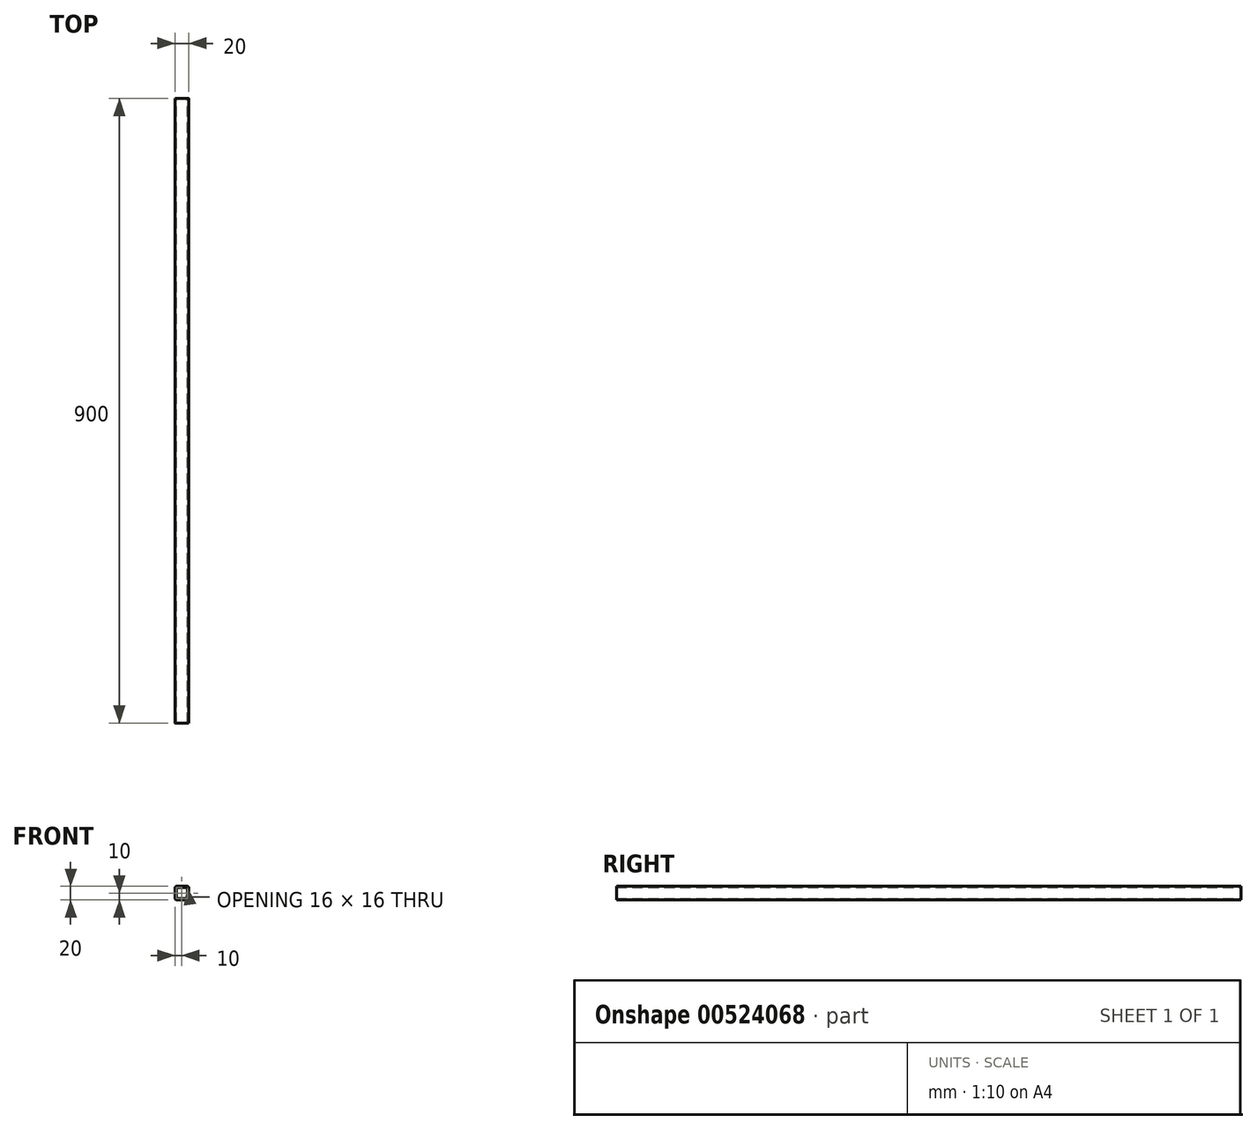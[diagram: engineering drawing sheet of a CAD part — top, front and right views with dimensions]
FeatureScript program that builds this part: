
annotation { "Feature Type Name" : "Feature", "Feature Type Description" : "" }
export const myFeature = defineFeature(function(context is Context, id is Id, definition is map)
    precondition{}
    {
        {
            assignVariable(context, id + "F0", {"name" : "R", "anyValue" : 3});
        }
        {
            assignVariable(context, id + "F1", {"name" : "W", "anyValue" : 2});
        }
        {
            var Q0;
            Q0=qCreatedBy(makeId("Front.planeOp"),FACE);
            var sketch = newSketch(context, id + "F2", { "sketchPlane" : qUnion([Q0])});
            skLineSegment(sketch, "E0.bottom", {"start": v(-10, 10) * mm, "end": v(10, 10) * mm});
            skLineSegment(sketch, "E0.top", {"start": v(-10, -10) * mm, "end": v(10, -10) * mm});
            skLineSegment(sketch, "E0.left", {"start": v(-10, 10) * mm, "end": v(-10, -10) * mm});
            skLineSegment(sketch, "E0.right", {"start": v(10, 10) * mm, "end": v(10, -10) * mm});
            skSolve(sketch);
        }
        {
            var Q0;
            Q0 = qSketchRegion(id + "F2", true);
            extrude(context, id + "F3", {"entities" : qUnion([Q0]), "endBound" : BoundingType.SYMMETRIC, "depth" : 900 * mm, "offsetDistance" : 25 * mm});
        }
        {
            var Q0;
            Q0=makeQuery(id+"F3.opExtrude","SWEPT_EDGE",EDGE,{"disambiguationData":[OSD([sQuery(id+"F2.wireOp",EDGE,"E0.bottom"),sQuery(id+"F2.wireOp",EDGE,"E0.right")])]});
            var Q1;
            Q1=makeQuery(id+"F3.opExtrude","SWEPT_EDGE",EDGE,{"disambiguationData":[OSD([sQuery(id+"F2.wireOp",EDGE,"E0.bottom"),sQuery(id+"F2.wireOp",EDGE,"E0.left")])]});
            var Q2;
            Q2=makeQuery(id+"F3.opExtrude","SWEPT_EDGE",EDGE,{"disambiguationData":[OSD([sQuery(id+"F2.wireOp",EDGE,"E0.top"),sQuery(id+"F2.wireOp",EDGE,"E0.right")])]});
            var Q3;
            Q3=makeQuery(id+"F3.opExtrude","SWEPT_EDGE",EDGE,{"disambiguationData":[OSD([sQuery(id+"F2.wireOp",EDGE,"E0.top"),sQuery(id+"F2.wireOp",EDGE,"E0.left")])]});
            fillet(context, id + "F4", {"entities" : qUnion([Q0, Q1, Q2, Q3]), "radius" : (getVariable(context, 'R')) * mm, "tangentPropagation" : true, "allowEdgeOverflow" : false});
        }
        {
            var Q0;
            Q0=makeQuery(id+"F3.opExtrude","CAP_FACE",FACE,{"disambiguationData":[OSD([sQuery(id+"F2.wireOp",EDGE,"E0.bottom"),sQuery(id+"F2.wireOp",EDGE,"E0.top"),sQuery(id+"F2.wireOp",EDGE,"E0.left"),sQuery(id+"F2.wireOp",EDGE,"E0.right")])],"isStart":false});
            var Q1;
            Q1=makeQuery(id+"F3.opExtrude","CAP_FACE",FACE,{"disambiguationData":[OSD([sQuery(id+"F2.wireOp",EDGE,"E0.bottom"),sQuery(id+"F2.wireOp",EDGE,"E0.top"),sQuery(id+"F2.wireOp",EDGE,"E0.left"),sQuery(id+"F2.wireOp",EDGE,"E0.right")])],"isStart":true});
            shell(context, id + "F5", {"entities" : qUnion([Q0, Q1]), "thickness" : (getVariable(context, 'W')) * mm});
        }
    });
